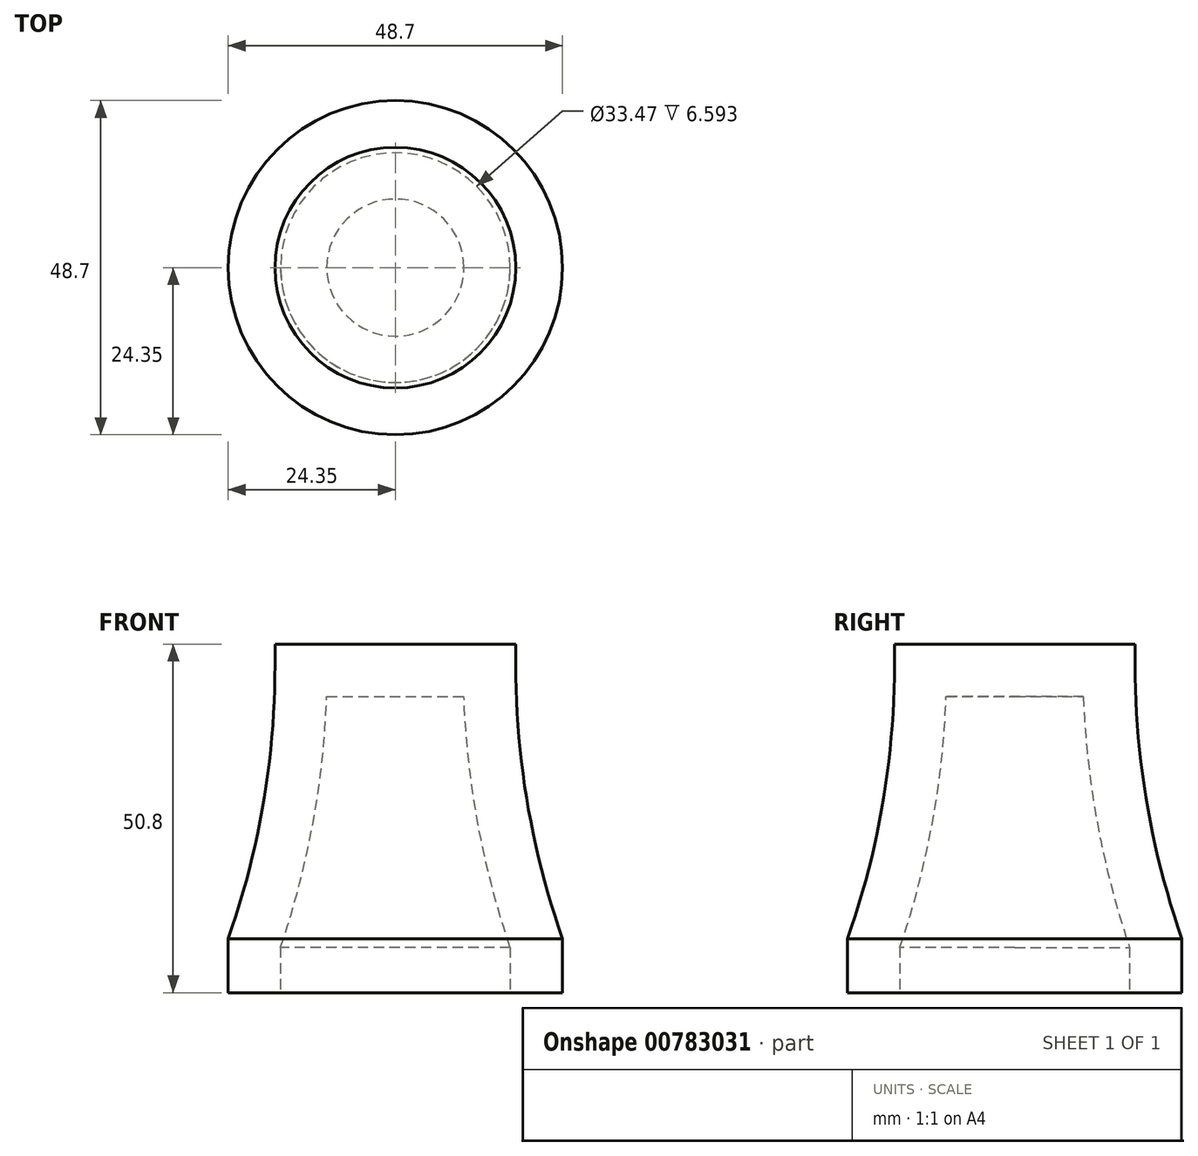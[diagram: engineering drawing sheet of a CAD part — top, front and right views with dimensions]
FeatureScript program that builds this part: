
annotation { "Feature Type Name" : "Feature", "Feature Type Description" : "" }
export const myFeature = defineFeature(function(context is Context, id is Id, definition is map)
    precondition{}
    {
        {
            var Q0;
            Q0=qCreatedBy(makeId("Top.planeOp"),FACE);
            var sketch = newSketch(context, id + "F0", { "sketchPlane" : qUnion([Q0])});
            skCircle(sketch, "E0", {"center": v(0, 0) * mm, "radius": 17.53 * mm});
            skSolve(sketch);
        }
        {
            var Q0;
            Q0 = qSketchRegion(id + "F0", true);
            extrude(context, id + "F1", {"entities" : qUnion([Q0]), "depth" : 50.8 * mm, "offsetDistance" : 25.4 * mm});
        }
        {
            var Q0;
            Q0=qCreatedBy(makeId("Top.planeOp"),FACE);
            var sketch = newSketch(context, id + "F2", { "sketchPlane" : qUnion([Q0])});
            skCircle(sketch, "E1", {"center": v(0, 0) * mm, "radius": 24.35 * mm});
            skSolve(sketch);
        }
        {
            var Q0;
            Q0 = qSketchRegion(id + "F2", true);
            extrude(context, id + "F3", {"entities" : qUnion([Q0]), "operationType" : NewBodyOperationType.ADD, "depth" : 7.87 * mm, "offsetDistance" : 25.4 * mm});
        }
        {
            var Q0;
            Q0=makeQuery(id+"F3.boolean.opBoolean","INTERSECT",EDGE,{"derivedFrom":[makeQuery(id+"F1.opExtrude","SWEPT_FACE",FACE,{"disambiguationData":[OSD([sQuery(id+"F0.wireOp",EDGE,"E0")])]}),makeQuery(id+"F3.opExtrude","CAP_FACE",FACE,{"disambiguationData":[OSD([sQuery(id+"F2.wireOp",EDGE,"E1")])],"isStart":false})]});
            fillet(context, id + "F4", {"entities" : qUnion([Q0]), "radius" : 120.19 * mm, "tangentPropagation" : true, "allowEdgeOverflow" : false});
        }
        {
            var Q0;
            Q0=makeQuery(id+"F3.boolean.opBoolean","MERGE",FACE,{"derivedFrom":[makeQuery(id+"F1.opExtrude","CAP_FACE",FACE,{"disambiguationData":[OSD([sQuery(id+"F0.wireOp",EDGE,"E0")])],"isStart":true}),makeQuery(id+"F3.opExtrude","CAP_FACE",FACE,{"disambiguationData":[OSD([sQuery(id+"F2.wireOp",EDGE,"E1")])],"isStart":true})]});
            shell(context, id + "F5", {"entities" : qUnion([Q0]), "thickness" : 7.62 * mm});
        }
    });
